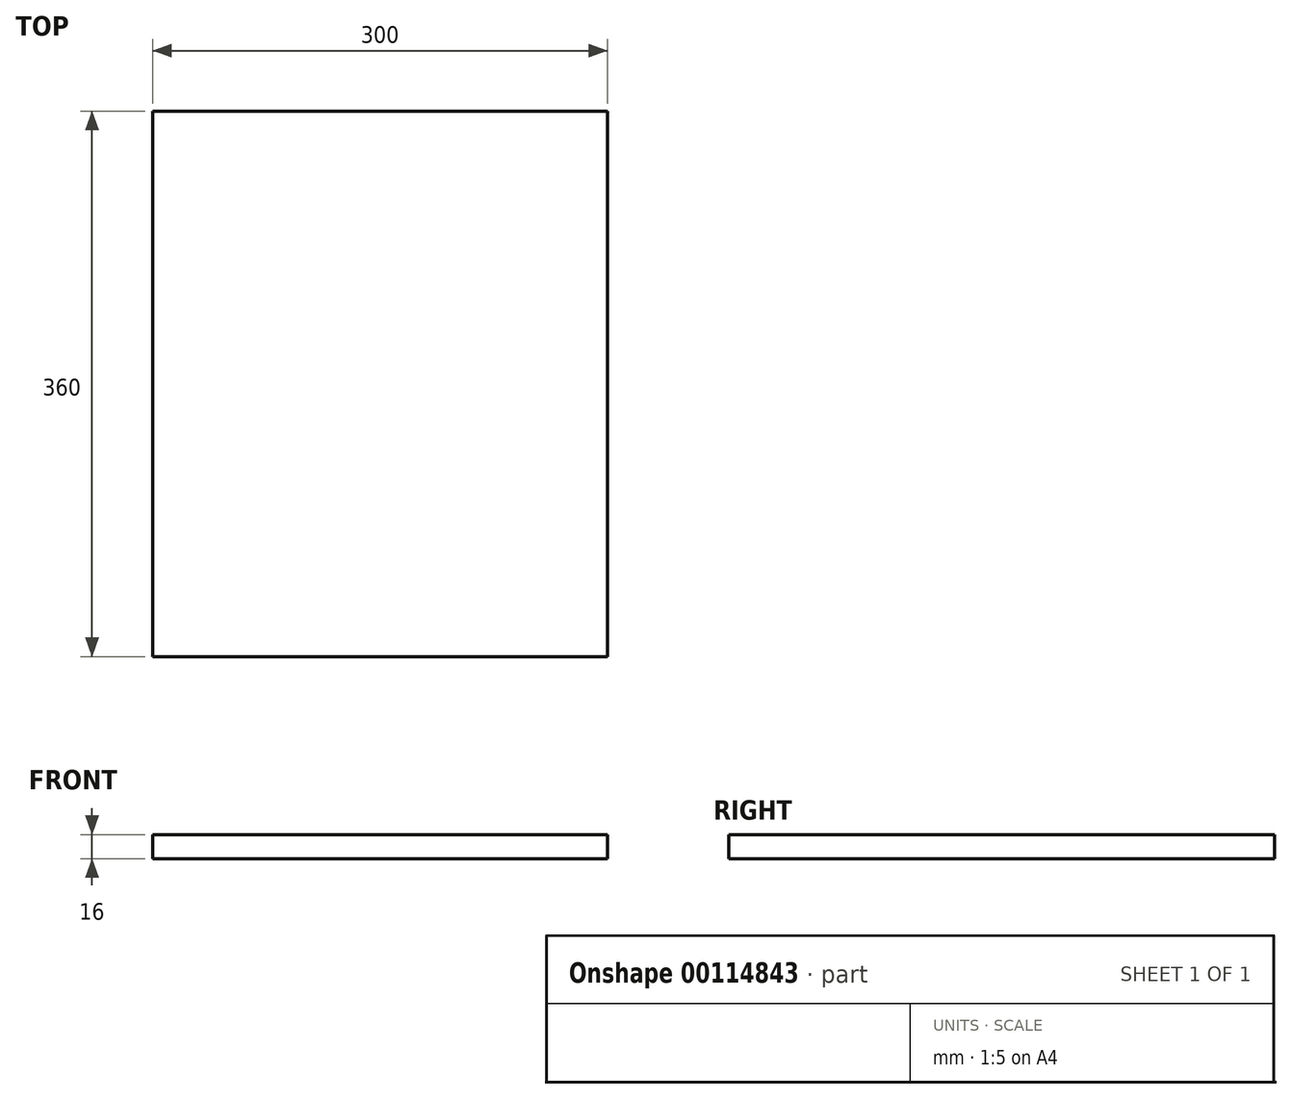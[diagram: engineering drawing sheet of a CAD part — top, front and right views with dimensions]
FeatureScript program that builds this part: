
annotation { "Feature Type Name" : "Feature", "Feature Type Description" : "" }
export const myFeature = defineFeature(function(context is Context, id is Id, definition is map)
    precondition{}
    {
        {
            var Q0;
            Q0=qCreatedBy(makeId("Top.planeOp"),FACE);
            var sketch = newSketch(context, id + "F0", { "sketchPlane" : qUnion([Q0])});
            skLineSegment(sketch, "E0.bottom", {"start": v(-150, 180) * mm, "end": v(150, 180) * mm});
            skLineSegment(sketch, "E0.top", {"start": v(-150, -180) * mm, "end": v(150, -180) * mm});
            skLineSegment(sketch, "E0.left", {"start": v(-150, 180) * mm, "end": v(-150, -180) * mm});
            skLineSegment(sketch, "E0.right", {"start": v(150, 180) * mm, "end": v(150, -180) * mm});
            skPoint(sketch, "E0.middle", {"position": v(0, 0) * mm});
            skSolve(sketch);
        }
        {
            var Q0;
            Q0=makeQuery(id+"F0.imprint","IMPRINT",FACE,{"disambiguationData":[TD([[makeQuery(id+"F0.imprint","IMPRINT",EDGE,{"derivedFrom":sQuery(id+"F0.wireOp",EDGE,"E0.bottom")}),-1.0]])]});
            extrude(context, id + "F1", {"entities" : qUnion([Q0]), "endBound" : BoundingType.SYMMETRIC, "depth" : 16 * mm});
        }
    });
